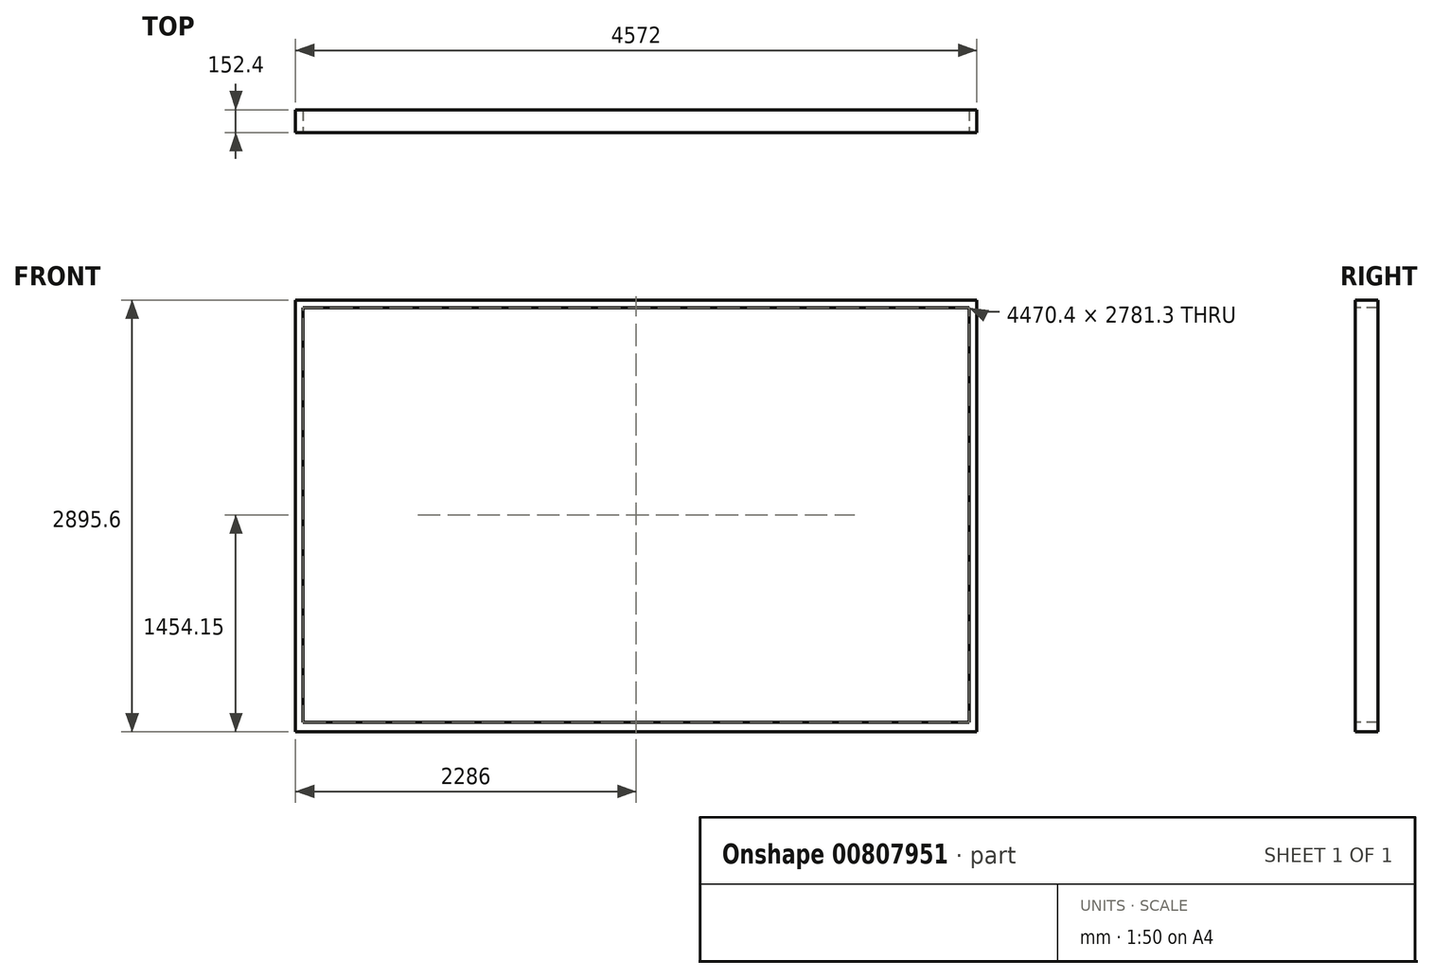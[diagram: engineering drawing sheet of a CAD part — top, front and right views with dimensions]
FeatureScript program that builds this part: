
annotation { "Feature Type Name" : "Feature", "Feature Type Description" : "" }
export const myFeature = defineFeature(function(context is Context, id is Id, definition is map)
    precondition{}
    {
        {
            var Q0;
            Q0=qCreatedBy(makeId("Front.planeOp"),FACE);
            var sketch = newSketch(context, id + "F0", { "sketchPlane" : qUnion([Q0])});
            skLineSegment(sketch, "E0.bottom", {"start": v(-2286, 1447.8) * mm, "end": v(2286, 1447.8) * mm});
            skLineSegment(sketch, "E0.top", {"start": v(-2286, -1447.8) * mm, "end": v(2286, -1447.8) * mm});
            skLineSegment(sketch, "E0.left", {"start": v(-2286, 1447.8) * mm, "end": v(-2286, -1447.8) * mm});
            skLineSegment(sketch, "E0.right", {"start": v(2286, 1447.8) * mm, "end": v(2286, -1447.8) * mm});
            skLineSegment(sketch, "E1", {"start": v(0, 1447.8) * mm, "end": v(0, 0) * mm, "construction": true});
            skLineSegment(sketch, "E2", {"start": v(0, 0) * mm, "end": v(-2286, 0) * mm, "construction": true});
            skSolve(sketch);
        }
        {
            var Q0;
            Q0=makeQuery(id+"F0.imprint","IMPRINT",FACE,{"disambiguationData":[TD([[makeQuery(id+"F0.imprint","IMPRINT",EDGE,{"derivedFrom":sQuery(id+"F0.wireOp",EDGE,"E0.bottom")}),-1.0]])]});
            extrude(context, id + "F1", {"entities" : qUnion([Q0]), "depth" : 152.4 * mm, "offsetDistance" : 25.4 * mm});
        }
        {
            var Q0;
            Q0=makeQuery(id+"F1.opExtrude","CAP_FACE",FACE,{"disambiguationData":[OSD([sQuery(id+"F0.wireOp",EDGE,"E0.bottom"),sQuery(id+"F0.wireOp",EDGE,"E0.top"),sQuery(id+"F0.wireOp",EDGE,"E0.left"),sQuery(id+"F0.wireOp",EDGE,"E0.right")])],"isStart":false});
            var sketch = newSketch(context, id + "F2", { "sketchPlane" : qUnion([Q0])});
            skLineSegment(sketch, "E3.bottom", {"start": v(-2235.2, 1397) * mm, "end": v(2235.2, 1397) * mm});
            skLineSegment(sketch, "E3.top", {"start": v(-2235.2, -1384.3) * mm, "end": v(2235.2, -1384.3) * mm});
            skLineSegment(sketch, "E3.left", {"start": v(-2235.2, 1397) * mm, "end": v(-2235.2, -1384.3) * mm});
            skLineSegment(sketch, "E3.right", {"start": v(2235.2, 1397) * mm, "end": v(2235.2, -1384.3) * mm});
            skSolve(sketch);
        }
        {
            var Q0;
            Q0=qSketchRegion(id+"F2",true);
            extrude(context, id + "F3", {"entities" : qUnion([Q0]), "operationType" : NewBodyOperationType.REMOVE, "endBound" : BoundingType.THROUGH_ALL, "oppositeDirection" : true, "depth" : 25.4 * mm, "offsetDistance" : 25.4 * mm});
        }
    });
